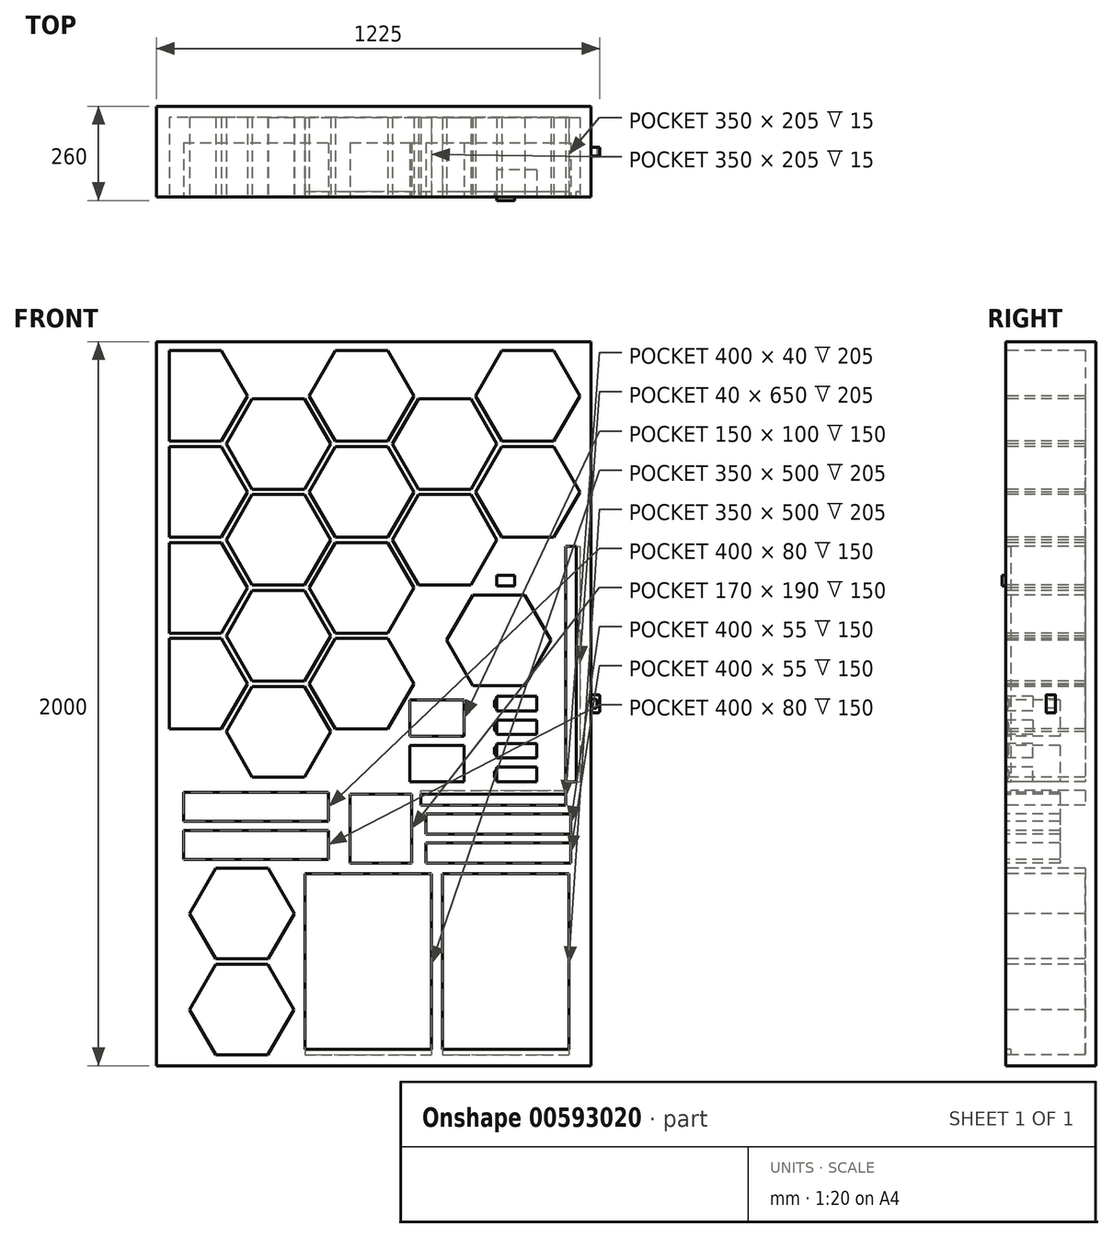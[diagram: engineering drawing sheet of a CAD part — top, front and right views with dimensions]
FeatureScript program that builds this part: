
annotation { "Feature Type Name" : "Feature", "Feature Type Description" : "" }
export const myFeature = defineFeature(function(context is Context, id is Id, definition is map)
    precondition{}
    {
        {
            var Q0;
            Q0=qCreatedBy(makeId("Top.planeOp"),FACE);
            var sketch = newSketch(context, id + "F0", { "sketchPlane" : qUnion([Q0])});
            skLineSegment(sketch, "E0.bottom", {"start": v(-593.08, -131.45) * mm, "end": v(606.92, -131.45) * mm});
            skLineSegment(sketch, "E0.top", {"start": v(-593.08, 118.55) * mm, "end": v(606.92, 118.55) * mm});
            skLineSegment(sketch, "E0.left", {"start": v(-593.08, -131.45) * mm, "end": v(-593.08, 118.55) * mm});
            skLineSegment(sketch, "E0.right", {"start": v(606.92, -131.45) * mm, "end": v(606.92, 118.55) * mm});
            skSolve(sketch);
        }
        {
            var Q0;
            Q0 = qSketchRegion(id + "F0", true);
            extrude(context, id + "F1", {"entities" : qUnion([Q0]), "depth" : 2000 * mm, "offsetDistance" : 25 * mm});
        }
        {
            var Q0;
            Q0=makeQuery(id+"F1.opExtrude","SWEPT_FACE",FACE,{"disambiguationData":[OSD([sQuery(id+"F0.wireOp",EDGE,"E0.bottom")])]});
            var sketch = newSketch(context, id + "F2", { "sketchPlane" : qUnion([Q0])});
            skLineSegment(sketch, "E1.right", {"start": v(576.92, 1435) * mm, "end": v(576.92, 785) * mm});
            skLineSegment(sketch, "E2", {"start": v(536.92, 1435) * mm, "end": v(576.92, 1435) * mm});
            skLineSegment(sketch, "E3", {"start": v(536.92, 1435) * mm, "end": v(536.92, 785) * mm});
            skLineSegment(sketch, "E4", {"start": v(536.92, 785) * mm, "end": v(576.92, 785) * mm});
            skLineSegment(sketch, "E5.bottom", {"start": v(136.92, 760) * mm, "end": v(536.92, 760) * mm});
            skLineSegment(sketch, "E5.top", {"start": v(136.92, 720) * mm, "end": v(536.92, 720) * mm});
            skLineSegment(sketch, "E5.left", {"start": v(136.92, 760) * mm, "end": v(136.92, 720) * mm});
            skLineSegment(sketch, "E5.right", {"start": v(536.92, 760) * mm, "end": v(536.92, 720) * mm});
            skSolve(sketch);
        }
        {
            var Q0;
            Q0 = qSketchRegion(id + "F2", true);
            extrude(context, id + "F3", {"entities" : qUnion([Q0]), "operationType" : NewBodyOperationType.REMOVE, "oppositeDirection" : true, "depth" : 220 * mm, "offsetDistance" : 25 * mm});
        }
        {
            var Q0;
            Q0=makeQuery(id+"F1.opExtrude","SWEPT_FACE",FACE,{"disambiguationData":[OSD([sQuery(id+"F0.wireOp",EDGE,"E0.right")])]});
            cPlane(context, id + "F4", {"entities" : qUnion([Q0]), "cplaneType" : CPlaneType.OFFSET, "offset" : 30 * mm, "oppositeDirection" : true, "width" : 150 * mm, "height" : 150 * mm});
        }
        {
            var Q0;
            Q0=qCreatedBy(id+"F4.planeOp",FACE);
            var sketch = newSketch(context, id + "F5", { "sketchPlane" : qUnion([Q0])});
            skLineSegment(sketch, "E6.bottom", {"start": v(-131.45, 1435) * mm, "end": v(-116.45, 1435) * mm});
            skLineSegment(sketch, "E6.top", {"start": v(-131.45, 785) * mm, "end": v(-116.45, 785) * mm});
            skLineSegment(sketch, "E6.left", {"start": v(-131.45, 1435) * mm, "end": v(-131.45, 785) * mm});
            skLineSegment(sketch, "E6.right", {"start": v(-116.45, 1435) * mm, "end": v(-116.45, 785) * mm});
            skSolve(sketch);
        }
        {
            var Q0;
            Q0 = qSketchRegion(id + "F5", true);
            extrude(context, id + "F6", {"entities" : qUnion([Q0]), "operationType" : NewBodyOperationType.ADD, "oppositeDirection" : true, "depth" : 10 * mm, "offsetDistance" : 25 * mm});
        }
        {
            var Q0;
            Q0=makeQuery(id+"F0.imprint","IMPRINT",FACE,{"disambiguationData":[TD([[makeQuery(id+"F0.imprint","IMPRINT",EDGE,{"derivedFrom":sQuery(id+"F0.wireOp",EDGE,"E0.bottom")}),1.0]])]});
            cPlane(context, id + "F7", {"entities" : qUnion([Q0]), "cplaneType" : CPlaneType.OFFSET, "offset" : 760 * mm, "width" : 150 * mm, "height" : 150 * mm});
        }
        {
            var Q0;
            Q0=qCreatedBy(id+"F7.planeOp",FACE);
            var sketch = newSketch(context, id + "F8", { "sketchPlane" : qUnion([Q0])});
            skLineSegment(sketch, "E7.bottom", {"start": v(136.92, -131.45) * mm, "end": v(536.92, -131.45) * mm});
            skLineSegment(sketch, "E7.top", {"start": v(136.92, -116.45) * mm, "end": v(536.92, -116.45) * mm});
            skLineSegment(sketch, "E7.left", {"start": v(136.92, -131.45) * mm, "end": v(136.92, -116.45) * mm});
            skLineSegment(sketch, "E7.right", {"start": v(536.92, -131.45) * mm, "end": v(536.92, -116.45) * mm});
            skSolve(sketch);
        }
        {
            var Q0;
            Q0 = qSketchRegion(id + "F8", true);
            extrude(context, id + "F9", {"entities" : qUnion([Q0]), "operationType" : NewBodyOperationType.ADD, "oppositeDirection" : true, "depth" : 10 * mm, "offsetDistance" : 25 * mm});
        }
        {
            var Q0;
            Q0=makeQuery(id+"F2.imprint","IMPRINT",FACE,{"disambiguationData":[TD([[makeQuery(id+"F2.imprint","IMPRINT",EDGE,{"derivedFrom":sQuery(id+"F2.wireOp",EDGE,"E1.right")}),1.0]])]});
            var sketch = newSketch(context, id + "F10", { "sketchPlane" : qUnion([Q0])});
            skLineSegment(sketch, "E8.bottom", {"start": v(456.92, 785) * mm, "end": v(346.92, 785) * mm});
            skLineSegment(sketch, "E8.top", {"start": v(456.92, 825) * mm, "end": v(346.92, 825) * mm});
            skLineSegment(sketch, "E8.left", {"start": v(456.92, 785) * mm, "end": v(456.92, 825) * mm});
            skLineSegment(sketch, "E8.right", {"start": v(346.92, 785) * mm, "end": v(346.92, 825) * mm});
            skSolve(sketch);
        }
        {
            var Q0;
            Q0=makeQuery(id+"F10.imprint","IMPRINT",FACE,{"disambiguationData":[TD([[makeQuery(id+"F10.imprint","IMPRINT",EDGE,{"derivedFrom":sQuery(id+"F10.wireOp",EDGE,"E8.bottom")}),-1.0]])]});
            extrude(context, id + "F11", {"entities" : qUnion([Q0]), "operationType" : NewBodyOperationType.REMOVE, "oppositeDirection" : true, "depth" : 75 * mm, "offsetDistance" : 25 * mm});
        }
        {
            var Q0;
            Q0=makeQuery(id+"F0.imprint","IMPRINT",FACE,{"disambiguationData":[TD([[makeQuery(id+"F0.imprint","IMPRINT",EDGE,{"derivedFrom":sQuery(id+"F0.wireOp",EDGE,"E0.bottom")}),1.0]])]});
            cPlane(context, id + "F12", {"entities" : qUnion([Q0]), "cplaneType" : CPlaneType.OFFSET, "offset" : 805 * mm, "width" : 150 * mm, "height" : 150 * mm});
        }
        {
            var Q0;
            Q0=qCreatedBy(id+"F12.planeOp",FACE);
            var sketch = newSketch(context, id + "F13", { "sketchPlane" : qUnion([Q0])});
            skArc(sketch, "E9", {"start": v(346.92, -123.45) * mm, "mid": v(338.92, -127.45) * mm, "end": v(346.92, -131.45) * mm});
            skLineSegment(sketch, "E10.bottom", {"start": v(346.92, -123.45) * mm, "end": v(351.44, -123.45) * mm});
            skLineSegment(sketch, "E10.top", {"start": v(346.92, -131.45) * mm, "end": v(351.44, -131.45) * mm});
            skLineSegment(sketch, "E10.right", {"start": v(351.44, -123.45) * mm, "end": v(351.44, -131.45) * mm});
            skSolve(sketch);
        }
        {
            var Q0;
            Q0 = qSketchRegion(id + "F13", true);
            var Q1;
            Q1=sQuery(id+"F13.wireOp",EDGE,"E9");
            var Q2;
            Q2=sQuery(id+"F13.wireOp",EDGE,"wPp1E5a5-Cfel-xhtf-EEdg-7zQgNDPYHGg3");
            extrude(context, id + "F14", {"entities" : qUnion([Q0]), "operationType" : NewBodyOperationType.REMOVE, "surfaceEntities" : qUnion([Q1, Q2]), "endBound" : BoundingType.SYMMETRIC, "oppositeDirection" : true, "depth" : 18 * mm, "offsetDistance" : 25 * mm, "hasDraft" : true, "draftAngle" : 0 * degree});
        }
        {
            var Q0;
            Q0=makeQuery(id+"F0.imprint","IMPRINT",FACE,{"disambiguationData":[TD([[makeQuery(id+"F0.imprint","IMPRINT",EDGE,{"derivedFrom":sQuery(id+"F0.wireOp",EDGE,"E0.bottom")}),1.0]])]});
            cPlane(context, id + "F15", {"entities" : qUnion([Q0]), "cplaneType" : CPlaneType.OFFSET, "offset" : 814 * mm, "width" : 150 * mm, "height" : 150 * mm});
        }
        {
            var Q0;
            Q0=makeQuery(id+"F0.imprint","IMPRINT",FACE,{"disambiguationData":[TD([[makeQuery(id+"F0.imprint","IMPRINT",EDGE,{"derivedFrom":sQuery(id+"F0.wireOp",EDGE,"E0.bottom")}),1.0]])]});
            cPlane(context, id + "F16", {"entities" : qUnion([Q0]), "cplaneType" : CPlaneType.OFFSET, "offset" : 796 * mm, "width" : 150 * mm, "height" : 150 * mm});
        }
        {
            var Q0;
            Q0=qCreatedBy(id+"F15.planeOp",FACE);
            var sketch = newSketch(context, id + "F17", { "sketchPlane" : qUnion([Q0])});
            skCircle(sketch, "E11", {"center": v(343.92, -127.45) * mm, "radius": 2.25 * mm});
            skSolve(sketch);
        }
        {
            var Q0;
            Q0 = qSketchRegion(id + "F17", true);
            extrude(context, id + "F18", {"entities" : qUnion([Q0]), "operationType" : NewBodyOperationType.REMOVE, "depth" : 5 * mm, "offsetDistance" : 25 * mm});
        }
        {
            var Q0;
            Q0=qCreatedBy(id+"F16.planeOp",FACE);
            var sketch = newSketch(context, id + "F19", { "sketchPlane" : qUnion([Q0])});
            skCircle(sketch, "E12", {"center": v(343.92, -127.45) * mm, "radius": 2.25 * mm});
            skSolve(sketch);
        }
        {
            var Q0;
            Q0 = qSketchRegion(id + "F19", true);
            extrude(context, id + "F20", {"entities" : qUnion([Q0]), "operationType" : NewBodyOperationType.REMOVE, "oppositeDirection" : true, "depth" : 5 * mm, "offsetDistance" : 25 * mm});
        }
        {
            var Q0;
            Q0=makeQuery(id+"F2.imprint","IMPRINT",FACE,{"disambiguationData":[TD([[makeQuery(id+"F2.imprint","IMPRINT",EDGE,{"derivedFrom":sQuery(id+"F2.wireOp",EDGE,"E1.right")}),1.0]])]});
            var sketch = newSketch(context, id + "F21", { "sketchPlane" : qUnion([Q0])});
            skLineSegment(sketch, "E13.bottom", {"start": v(456.92, 850) * mm, "end": v(346.92, 850) * mm});
            skLineSegment(sketch, "E13.top", {"start": v(456.92, 890) * mm, "end": v(346.92, 890) * mm});
            skLineSegment(sketch, "E13.left", {"start": v(456.92, 850) * mm, "end": v(456.92, 890) * mm});
            skLineSegment(sketch, "E13.right", {"start": v(346.92, 850) * mm, "end": v(346.92, 890) * mm});
            skSolve(sketch);
        }
        {
            var Q0;
            Q0 = qSketchRegion(id + "F21", true);
            var Q1;
            Q1=sQuery(id+"F21.wireOp",EDGE,"E13.top");
            extrude(context, id + "F22", {"entities" : qUnion([Q0]), "operationType" : NewBodyOperationType.REMOVE, "surfaceEntities" : qUnion([Q1]), "oppositeDirection" : true, "depth" : 75 * mm, "offsetDistance" : 25 * mm});
        }
        {
            var Q0;
            Q0=makeQuery(id+"F0.imprint","IMPRINT",FACE,{"disambiguationData":[TD([[makeQuery(id+"F0.imprint","IMPRINT",EDGE,{"derivedFrom":sQuery(id+"F0.wireOp",EDGE,"E0.bottom")}),1.0]])]});
            cPlane(context, id + "F23", {"entities" : qUnion([Q0]), "cplaneType" : CPlaneType.OFFSET, "offset" : 870 * mm, "width" : 150 * mm, "height" : 150 * mm});
        }
        {
            var Q0;
            Q0=qCreatedBy(id+"F23.planeOp",FACE);
            var sketch = newSketch(context, id + "F24", { "sketchPlane" : qUnion([Q0])});
            skArc(sketch, "E14", {"start": v(346.92, -123.45) * mm, "mid": v(338.92, -127.45) * mm, "end": v(346.92, -131.45) * mm});
            skLineSegment(sketch, "E15.bottom", {"start": v(346.92, -123.45) * mm, "end": v(351.44, -123.45) * mm});
            skLineSegment(sketch, "E15.top", {"start": v(346.92, -131.45) * mm, "end": v(351.44, -131.45) * mm});
            skLineSegment(sketch, "E15.right", {"start": v(351.44, -123.45) * mm, "end": v(351.44, -131.45) * mm});
            skSolve(sketch);
        }
        {
            var Q0;
            Q0 = qSketchRegion(id + "F24", true);
            extrude(context, id + "F25", {"entities" : qUnion([Q0]), "operationType" : NewBodyOperationType.REMOVE, "endBound" : BoundingType.SYMMETRIC, "oppositeDirection" : true, "depth" : 18 * mm, "offsetDistance" : 25 * mm});
        }
        {
            var Q0;
            Q0=makeQuery(id+"F0.imprint","IMPRINT",FACE,{"disambiguationData":[TD([[makeQuery(id+"F0.imprint","IMPRINT",EDGE,{"derivedFrom":sQuery(id+"F0.wireOp",EDGE,"E0.bottom")}),1.0]])]});
            cPlane(context, id + "F26", {"entities" : qUnion([Q0]), "cplaneType" : CPlaneType.OFFSET, "offset" : 879 * mm, "width" : 150 * mm, "height" : 150 * mm});
        }
        {
            var Q0;
            Q0=makeQuery(id+"F0.imprint","IMPRINT",FACE,{"disambiguationData":[TD([[makeQuery(id+"F0.imprint","IMPRINT",EDGE,{"derivedFrom":sQuery(id+"F0.wireOp",EDGE,"E0.bottom")}),1.0]])]});
            cPlane(context, id + "F27", {"entities" : qUnion([Q0]), "cplaneType" : CPlaneType.OFFSET, "offset" : 861 * mm, "width" : 150 * mm, "height" : 150 * mm});
        }
        {
            var Q0;
            Q0=qCreatedBy(id+"F26.planeOp",FACE);
            var sketch = newSketch(context, id + "F28", { "sketchPlane" : qUnion([Q0])});
            skCircle(sketch, "E16", {"center": v(343.92, -127.45) * mm, "radius": 2.25 * mm});
            skSolve(sketch);
        }
        {
            var Q0;
            Q0 = qSketchRegion(id + "F28", true);
            extrude(context, id + "F29", {"entities" : qUnion([Q0]), "operationType" : NewBodyOperationType.REMOVE, "depth" : 5 * mm, "offsetDistance" : 25 * mm});
        }
        {
            var Q0;
            Q0=qCreatedBy(id+"F27.planeOp",FACE);
            var sketch = newSketch(context, id + "F30", { "sketchPlane" : qUnion([Q0])});
            skCircle(sketch, "E17", {"center": v(343.92, -127.45) * mm, "radius": 2.25 * mm});
            skSolve(sketch);
        }
        {
            var Q0;
            Q0 = qSketchRegion(id + "F30", true);
            extrude(context, id + "F31", {"entities" : qUnion([Q0]), "operationType" : NewBodyOperationType.REMOVE, "oppositeDirection" : true, "depth" : 5 * mm, "offsetDistance" : 25 * mm});
        }
        {
            var Q0;
            Q0=makeQuery(id+"F2.imprint","IMPRINT",FACE,{"disambiguationData":[TD([[makeQuery(id+"F2.imprint","IMPRINT",EDGE,{"derivedFrom":sQuery(id+"F2.wireOp",EDGE,"E1.right")}),1.0]])]});
            var sketch = newSketch(context, id + "F32", { "sketchPlane" : qUnion([Q0])});
            skLineSegment(sketch, "E18.bottom", {"start": v(346.92, 955) * mm, "end": v(456.92, 955) * mm});
            skLineSegment(sketch, "E18.top", {"start": v(346.92, 915) * mm, "end": v(456.92, 915) * mm});
            skLineSegment(sketch, "E18.left", {"start": v(346.92, 955) * mm, "end": v(346.92, 915) * mm});
            skLineSegment(sketch, "E18.right", {"start": v(456.92, 955) * mm, "end": v(456.92, 915) * mm});
            skSolve(sketch);
        }
        {
            var Q0;
            Q0 = qSketchRegion(id + "F32", true);
            extrude(context, id + "F33", {"entities" : qUnion([Q0]), "operationType" : NewBodyOperationType.REMOVE, "oppositeDirection" : true, "depth" : 75 * mm, "offsetDistance" : 25 * mm});
        }
        {
            var Q0;
            Q0=makeQuery(id+"F0.imprint","IMPRINT",FACE,{"disambiguationData":[TD([[makeQuery(id+"F0.imprint","IMPRINT",EDGE,{"derivedFrom":sQuery(id+"F0.wireOp",EDGE,"E0.bottom")}),1.0]])]});
            cPlane(context, id + "F34", {"entities" : qUnion([Q0]), "cplaneType" : CPlaneType.OFFSET, "offset" : 935 * mm, "width" : 150 * mm, "height" : 150 * mm});
        }
        {
            var Q0;
            Q0=qCreatedBy(id+"F34.planeOp",FACE);
            var sketch = newSketch(context, id + "F35", { "sketchPlane" : qUnion([Q0])});
            skArc(sketch, "E19", {"start": v(346.92, -123.45) * mm, "mid": v(338.92, -127.45) * mm, "end": v(346.92, -131.45) * mm});
            skLineSegment(sketch, "E20", {"start": v(346.92, -123.45) * mm, "end": v(346.92, -131.45) * mm});
            skSolve(sketch);
        }
        {
            var Q0;
            Q0 = qSketchRegion(id + "F35", true);
            extrude(context, id + "F36", {"entities" : qUnion([Q0]), "operationType" : NewBodyOperationType.REMOVE, "endBound" : BoundingType.SYMMETRIC, "oppositeDirection" : true, "depth" : 18 * mm, "offsetDistance" : 25 * mm});
        }
        {
            var Q0;
            Q0=makeQuery(id+"F0.imprint","IMPRINT",FACE,{"disambiguationData":[TD([[makeQuery(id+"F0.imprint","IMPRINT",EDGE,{"derivedFrom":sQuery(id+"F0.wireOp",EDGE,"E0.bottom")}),1.0]])]});
            cPlane(context, id + "F37", {"entities" : qUnion([Q0]), "cplaneType" : CPlaneType.OFFSET, "offset" : 944 * mm, "width" : 150 * mm, "height" : 150 * mm});
        }
        {
            var Q0;
            Q0=makeQuery(id+"F0.imprint","IMPRINT",FACE,{"disambiguationData":[TD([[makeQuery(id+"F0.imprint","IMPRINT",EDGE,{"derivedFrom":sQuery(id+"F0.wireOp",EDGE,"E0.bottom")}),1.0]])]});
            cPlane(context, id + "F38", {"entities" : qUnion([Q0]), "cplaneType" : CPlaneType.OFFSET, "offset" : 926 * mm, "width" : 150 * mm, "height" : 150 * mm});
        }
        {
            var Q0;
            Q0=qCreatedBy(id+"F37.planeOp",FACE);
            var sketch = newSketch(context, id + "F39", { "sketchPlane" : qUnion([Q0])});
            skCircle(sketch, "E21", {"center": v(343.92, -127.45) * mm, "radius": 2.25 * mm});
            skSolve(sketch);
        }
        {
            var Q0;
            Q0 = qSketchRegion(id + "F39", true);
            extrude(context, id + "F40", {"entities" : qUnion([Q0]), "operationType" : NewBodyOperationType.REMOVE, "depth" : 5 * mm, "offsetDistance" : 25 * mm});
        }
        {
            var Q0;
            Q0=qCreatedBy(id+"F38.planeOp",FACE);
            var sketch = newSketch(context, id + "F41", { "sketchPlane" : qUnion([Q0])});
            skCircle(sketch, "E22", {"center": v(343.92, -127.45) * mm, "radius": 2.25 * mm});
            skSolve(sketch);
        }
        {
            var Q0;
            Q0 = qSketchRegion(id + "F41", true);
            extrude(context, id + "F42", {"entities" : qUnion([Q0]), "operationType" : NewBodyOperationType.REMOVE, "oppositeDirection" : true, "depth" : 5 * mm, "offsetDistance" : 25 * mm});
        }
        {
            var Q0;
            Q0=makeQuery(id+"F2.imprint","IMPRINT",FACE,{"disambiguationData":[TD([[makeQuery(id+"F2.imprint","IMPRINT",EDGE,{"derivedFrom":sQuery(id+"F2.wireOp",EDGE,"E1.right")}),1.0]])]});
            var sketch = newSketch(context, id + "F43", { "sketchPlane" : qUnion([Q0])});
            skLineSegment(sketch, "E23.bottom", {"start": v(546.92, 30) * mm, "end": v(196.92, 30) * mm});
            skLineSegment(sketch, "E23.top", {"start": v(546.92, 530) * mm, "end": v(196.92, 530) * mm});
            skLineSegment(sketch, "E23.left", {"start": v(546.92, 30) * mm, "end": v(546.92, 530) * mm});
            skLineSegment(sketch, "E23.right", {"start": v(196.92, 30) * mm, "end": v(196.92, 530) * mm});
            skLineSegment(sketch, "E24.bottom", {"start": v(-183.08, 530) * mm, "end": v(166.92, 530) * mm});
            skLineSegment(sketch, "E24.top", {"start": v(-183.08, 30) * mm, "end": v(166.92, 30) * mm});
            skLineSegment(sketch, "E24.left", {"start": v(-183.08, 530) * mm, "end": v(-183.08, 30) * mm});
            skLineSegment(sketch, "E24.right", {"start": v(166.92, 530) * mm, "end": v(166.92, 30) * mm});
            skSolve(sketch);
        }
        {
            var Q0;
            Q0=makeQuery(id+"F43.imprint","IMPRINT",FACE,{"disambiguationData":[TD([[makeQuery(id+"F43.imprint","IMPRINT",EDGE,{"derivedFrom":sQuery(id+"F43.wireOp",EDGE,"E23.bottom")}),1.0]])]});
            var sketch = newSketch(context, id + "F44", { "sketchPlane" : qUnion([Q0])});
            skLineSegment(sketch, "E25.bottom", {"start": v(106.92, 1010) * mm, "end": v(256.92, 1010) * mm});
            skLineSegment(sketch, "E25.top", {"start": v(106.92, 785) * mm, "end": v(256.92, 785) * mm});
            skLineSegment(sketch, "E25.left", {"start": v(106.92, 1010) * mm, "end": v(106.92, 910) * mm});
            skLineSegment(sketch, "E25.right", {"start": v(256.92, 1010) * mm, "end": v(256.92, 910) * mm});
            skLineSegment(sketch, "E26", {"start": v(256.92, 910) * mm, "end": v(106.92, 910) * mm});
            skLineSegment(sketch, "E27", {"start": v(106.92, 885) * mm, "end": v(256.92, 885) * mm});
            skLineSegment(sketch, "E28.trimOffspring", {"start": v(106.92, 885) * mm, "end": v(106.92, 785) * mm});
            skLineSegment(sketch, "E29.trimOffspring", {"start": v(256.92, 885) * mm, "end": v(256.92, 785) * mm});
            skSolve(sketch);
        }
        {
            var Q0;
            Q0=makeQuery(id+"F44.imprint","IMPRINT",FACE,{"disambiguationData":[TD([[makeQuery(id+"F44.imprint","IMPRINT",EDGE,{"derivedFrom":sQuery(id+"F44.wireOp",EDGE,"E25.bottom")}),-1.0]])]});
            var Q1;
            Q1=makeQuery(id+"F44.imprint","IMPRINT",FACE,{"disambiguationData":[TD([[makeQuery(id+"F44.imprint","IMPRINT",EDGE,{"derivedFrom":sQuery(id+"F44.wireOp",EDGE,"E25.top")}),1.0]])]});
            extrude(context, id + "F45", {"entities" : qUnion([Q0, Q1]), "operationType" : NewBodyOperationType.REMOVE, "oppositeDirection" : true, "depth" : 150 * mm, "offsetDistance" : 25 * mm});
        }
        {
            var Q0;
            Q0=makeQuery(id+"F2.imprint","IMPRINT",FACE,{"disambiguationData":[TD([[makeQuery(id+"F2.imprint","IMPRINT",EDGE,{"derivedFrom":sQuery(id+"F2.wireOp",EDGE,"E1.right")}),1.0]])]});
            var sketch = newSketch(context, id + "F46", { "sketchPlane" : qUnion([Q0])});
            skCircle(sketch, "E30.cCircle", {"center": v(352.58, 1175) * mm, "radius": 125 * mm, "construction": true});
            skLineSegment(sketch, "E30.0", {"start": v(496.92, 1175) * mm, "end": v(424.75, 1050) * mm});
            skLineSegment(sketch, "E30.1", {"start": v(424.75, 1050) * mm, "end": v(280.4, 1050) * mm});
            skLineSegment(sketch, "E30.2", {"start": v(280.4, 1050) * mm, "end": v(208.24, 1175) * mm});
            skLineSegment(sketch, "E30.3", {"start": v(208.24, 1175) * mm, "end": v(280.4, 1300) * mm});
            skLineSegment(sketch, "E30.4", {"start": v(280.4, 1300) * mm, "end": v(424.75, 1300) * mm});
            skLineSegment(sketch, "E30.5", {"start": v(424.75, 1300) * mm, "end": v(496.92, 1175) * mm});
            skPoint(sketch, "E30.0.midPoint", {"position": v(460.83, 1112.5) * mm});
            skSolve(sketch);
        }
        {
            var Q0;
            Q0=makeQuery(id+"F46.imprint","IMPRINT",FACE,{"disambiguationData":[TD([[makeQuery(id+"F46.imprint","IMPRINT",EDGE,{"derivedFrom":sQuery(id+"F46.wireOp",EDGE,"E30.0")}),-1.0]])]});
            extrude(context, id + "F47", {"entities" : qUnion([Q0]), "operationType" : NewBodyOperationType.REMOVE, "oppositeDirection" : true, "depth" : 220 * mm, "offsetDistance" : 25 * mm});
        }
        {
            var Q0;
            Q0=makeQuery(id+"F0.imprint","IMPRINT",FACE,{"disambiguationData":[TD([[makeQuery(id+"F0.imprint","IMPRINT",EDGE,{"derivedFrom":sQuery(id+"F0.wireOp",EDGE,"E0.bottom")}),1.0]])]});
            cPlane(context, id + "F48", {"entities" : qUnion([Q0]), "cplaneType" : CPlaneType.OFFSET, "offset" : 1000 * mm, "width" : 150 * mm, "height" : 150 * mm});
        }
        {
            var Q0;
            Q0=makeQuery(id+"F2.imprint","IMPRINT",FACE,{"disambiguationData":[TD([[makeQuery(id+"F2.imprint","IMPRINT",EDGE,{"derivedFrom":sQuery(id+"F2.wireOp",EDGE,"E1.right")}),1.0]])]});
            var sketch = newSketch(context, id + "F49", { "sketchPlane" : qUnion([Q0])});
            skLineSegment(sketch, "E31.bottom", {"start": v(346.92, 1020) * mm, "end": v(456.92, 1020) * mm});
            skLineSegment(sketch, "E31.top", {"start": v(346.92, 980) * mm, "end": v(456.92, 980) * mm});
            skLineSegment(sketch, "E31.left", {"start": v(346.92, 1020) * mm, "end": v(346.92, 980) * mm});
            skLineSegment(sketch, "E31.right", {"start": v(456.92, 1020) * mm, "end": v(456.92, 980) * mm});
            skSolve(sketch);
        }
        {
            var Q0;
            Q0 = qSketchRegion(id + "F49", true);
            extrude(context, id + "F50", {"entities" : qUnion([Q0]), "operationType" : NewBodyOperationType.REMOVE, "oppositeDirection" : true, "depth" : 75 * mm, "offsetDistance" : 25 * mm});
        }
        {
            var Q0;
            Q0=qCreatedBy(id+"F48.planeOp",FACE);
            var sketch = newSketch(context, id + "F51", { "sketchPlane" : qUnion([Q0])});
            skArc(sketch, "E32", {"start": v(346.92, -123.45) * mm, "mid": v(338.92, -127.45) * mm, "end": v(346.92, -131.45) * mm});
            skLineSegment(sketch, "E33", {"start": v(346.92, -123.45) * mm, "end": v(346.92, -131.45) * mm});
            skSolve(sketch);
        }
        {
            var Q0;
            Q0 = qSketchRegion(id + "F51", true);
            extrude(context, id + "F52", {"entities" : qUnion([Q0]), "operationType" : NewBodyOperationType.REMOVE, "endBound" : BoundingType.SYMMETRIC, "depth" : 18 * mm, "offsetDistance" : 25 * mm});
        }
        {
            var Q0;
            Q0=makeQuery(id+"F0.imprint","IMPRINT",FACE,{"disambiguationData":[TD([[makeQuery(id+"F0.imprint","IMPRINT",EDGE,{"derivedFrom":sQuery(id+"F0.wireOp",EDGE,"E0.bottom")}),1.0]])]});
            cPlane(context, id + "F53", {"entities" : qUnion([Q0]), "cplaneType" : CPlaneType.OFFSET, "offset" : 1009 * mm, "width" : 150 * mm, "height" : 150 * mm});
        }
        {
            var Q0;
            Q0=makeQuery(id+"F0.imprint","IMPRINT",FACE,{"disambiguationData":[TD([[makeQuery(id+"F0.imprint","IMPRINT",EDGE,{"derivedFrom":sQuery(id+"F0.wireOp",EDGE,"E0.bottom")}),1.0]])]});
            cPlane(context, id + "F54", {"entities" : qUnion([Q0]), "cplaneType" : CPlaneType.OFFSET, "offset" : 991 * mm, "width" : 150 * mm, "height" : 150 * mm});
        }
        {
            var Q0;
            Q0=qCreatedBy(id+"F53.planeOp",FACE);
            var sketch = newSketch(context, id + "F55", { "sketchPlane" : qUnion([Q0])});
            skCircle(sketch, "E34", {"center": v(343.92, -127.45) * mm, "radius": 2.25 * mm});
            skSolve(sketch);
        }
        {
            var Q0;
            Q0 = qSketchRegion(id + "F55", true);
            extrude(context, id + "F56", {"entities" : qUnion([Q0]), "operationType" : NewBodyOperationType.REMOVE, "depth" : 5 * mm, "offsetDistance" : 25 * mm});
        }
        {
            var Q0;
            Q0=qCreatedBy(id+"F54.planeOp",FACE);
            var sketch = newSketch(context, id + "F57", { "sketchPlane" : qUnion([Q0])});
            skCircle(sketch, "E35", {"center": v(343.92, -127.45) * mm, "radius": 2.25 * mm});
            skSolve(sketch);
        }
        {
            var Q0;
            Q0 = qSketchRegion(id + "F57", true);
            extrude(context, id + "F58", {"entities" : qUnion([Q0]), "operationType" : NewBodyOperationType.REMOVE, "oppositeDirection" : true, "depth" : 5 * mm, "offsetDistance" : 25 * mm});
        }
        {
            var Q0;
            Q0=makeQuery(id+"F10.imprint","IMPRINT",FACE,{"disambiguationData":[TD([[makeQuery(id+"F10.imprint","IMPRINT",EDGE,{"derivedFrom":sQuery(id+"F10.wireOp",EDGE,"E8.bottom")}),1.0]])]});
            var sketch = newSketch(context, id + "F59", { "sketchPlane" : qUnion([Q0])});
            skLineSegment(sketch, "E36.bottom", {"start": v(346.92, 1355) * mm, "end": v(396.92, 1355) * mm});
            skLineSegment(sketch, "E36.top", {"start": v(346.92, 1325) * mm, "end": v(396.92, 1325) * mm});
            skLineSegment(sketch, "E36.left", {"start": v(346.92, 1355) * mm, "end": v(346.92, 1325) * mm});
            skLineSegment(sketch, "E36.right", {"start": v(396.92, 1355) * mm, "end": v(396.92, 1325) * mm});
            skSolve(sketch);
        }
        {
            var Q0;
            Q0 = qSketchRegion(id + "F59", true);
            extrude(context, id + "F60", {"entities" : qUnion([Q0]), "operationType" : NewBodyOperationType.ADD, "depth" : 10 * mm, "offsetDistance" : 25 * mm});
        }
        {
            var Q0;
            Q0 = qSketchRegion(id + "F43", true);
            extrude(context, id + "F61", {"entities" : qUnion([Q0]), "operationType" : NewBodyOperationType.REMOVE, "oppositeDirection" : true, "depth" : 220 * mm, "offsetDistance" : 25 * mm});
        }
        {
            var Q0;
            Q0=makeQuery(id+"F0.imprint","IMPRINT",FACE,{"disambiguationData":[TD([[makeQuery(id+"F0.imprint","IMPRINT",EDGE,{"derivedFrom":sQuery(id+"F0.wireOp",EDGE,"E0.bottom")}),1.0]])]});
            cPlane(context, id + "F62", {"entities" : qUnion([Q0]), "cplaneType" : CPlaneType.OFFSET, "offset" : 30 * mm, "width" : 150 * mm, "height" : 150 * mm});
        }
        {
            var Q0;
            Q0=qCreatedBy(id+"F62.planeOp",FACE);
            var sketch = newSketch(context, id + "F63", { "sketchPlane" : qUnion([Q0])});
            skLineSegment(sketch, "E37.bottom", {"start": v(-183.08, -116.45) * mm, "end": v(166.92, -116.45) * mm});
            skLineSegment(sketch, "E37.top", {"start": v(-183.08, -131.45) * mm, "end": v(166.92, -131.45) * mm});
            skLineSegment(sketch, "E37.left", {"start": v(-183.08, -116.45) * mm, "end": v(-183.08, -131.45) * mm});
            skLineSegment(sketch, "E37.right", {"start": v(166.92, -116.45) * mm, "end": v(166.92, -131.45) * mm});
            skLineSegment(sketch, "E38.bottom", {"start": v(196.92, -116.45) * mm, "end": v(546.92, -116.45) * mm});
            skLineSegment(sketch, "E38.top", {"start": v(196.92, -131.45) * mm, "end": v(546.92, -131.45) * mm});
            skLineSegment(sketch, "E38.left", {"start": v(196.92, -116.45) * mm, "end": v(196.92, -131.45) * mm});
            skLineSegment(sketch, "E38.right", {"start": v(546.92, -116.45) * mm, "end": v(546.92, -131.45) * mm});
            skSolve(sketch);
        }
        {
            var Q0;
            Q0 = qSketchRegion(id + "F63", true);
            extrude(context, id + "F64", {"entities" : qUnion([Q0]), "operationType" : NewBodyOperationType.ADD, "depth" : 15 * mm, "offsetDistance" : 25 * mm});
        }
        {
            var Q0;
            Q0=makeQuery(id+"F2.imprint","IMPRINT",FACE,{"disambiguationData":[TD([[makeQuery(id+"F2.imprint","IMPRINT",EDGE,{"derivedFrom":sQuery(id+"F2.wireOp",EDGE,"E1.right")}),1.0]])]});
            var sketch = newSketch(context, id + "F65", { "sketchPlane" : qUnion([Q0])});
            skCircle(sketch, "E39.cCircle", {"center": v(432.58, 1850) * mm, "radius": 125 * mm, "construction": true});
            skLineSegment(sketch, "E39.0", {"start": v(360.4, 1975) * mm, "end": v(288.24, 1850) * mm});
            skLineSegment(sketch, "E39.1", {"start": v(504.75, 1975) * mm, "end": v(360.4, 1975) * mm});
            skLineSegment(sketch, "E39.2", {"start": v(576.92, 1850) * mm, "end": v(504.75, 1975) * mm});
            skLineSegment(sketch, "E39.3", {"start": v(504.75, 1725) * mm, "end": v(576.92, 1850) * mm});
            skLineSegment(sketch, "E39.4", {"start": v(360.4, 1725) * mm, "end": v(504.75, 1725) * mm});
            skLineSegment(sketch, "E39.5", {"start": v(288.24, 1850) * mm, "end": v(360.4, 1725) * mm});
            skPoint(sketch, "E39.0.midPoint", {"position": v(324.32, 1912.5) * mm});
            skCircle(sketch, "E40.cCircle", {"center": v(203.08, 1717.5) * mm, "radius": 125 * mm, "construction": true});
            skLineSegment(sketch, "E40.0", {"start": v(130.91, 1842.5) * mm, "end": v(58.74, 1717.5) * mm});
            skLineSegment(sketch, "E40.1", {"start": v(275.25, 1842.5) * mm, "end": v(130.91, 1842.5) * mm});
            skLineSegment(sketch, "E40.2", {"start": v(347.42, 1717.5) * mm, "end": v(275.25, 1842.5) * mm});
            skLineSegment(sketch, "E40.3", {"start": v(275.25, 1592.5) * mm, "end": v(347.42, 1717.5) * mm});
            skLineSegment(sketch, "E40.4", {"start": v(130.91, 1592.5) * mm, "end": v(275.25, 1592.5) * mm});
            skLineSegment(sketch, "E40.5", {"start": v(58.74, 1717.5) * mm, "end": v(130.91, 1592.5) * mm});
            skPoint(sketch, "E40.0.midPoint", {"position": v(94.83, 1780) * mm});
            skCircle(sketch, "E41.cCircle", {"center": v(432.58, 1585) * mm, "radius": 125 * mm, "construction": true});
            skLineSegment(sketch, "E41.0", {"start": v(360.4, 1710) * mm, "end": v(288.24, 1585) * mm});
            skLineSegment(sketch, "E41.1", {"start": v(504.75, 1710) * mm, "end": v(360.4, 1710) * mm});
            skLineSegment(sketch, "E41.2", {"start": v(576.92, 1585) * mm, "end": v(504.75, 1710) * mm});
            skLineSegment(sketch, "E41.3", {"start": v(504.75, 1460) * mm, "end": v(576.92, 1585) * mm});
            skLineSegment(sketch, "E41.4", {"start": v(360.4, 1460) * mm, "end": v(504.75, 1460) * mm});
            skLineSegment(sketch, "E41.5", {"start": v(288.24, 1585) * mm, "end": v(360.4, 1460) * mm});
            skPoint(sketch, "E41.0.midPoint", {"position": v(324.32, 1647.5) * mm});
            skCircle(sketch, "E42.cCircle", {"center": v(203.08, 1452.5) * mm, "radius": 125 * mm, "construction": true});
            skLineSegment(sketch, "E42.0", {"start": v(130.91, 1577.5) * mm, "end": v(58.74, 1452.5) * mm});
            skLineSegment(sketch, "E42.1", {"start": v(275.25, 1577.5) * mm, "end": v(130.91, 1577.5) * mm});
            skLineSegment(sketch, "E42.2", {"start": v(347.42, 1452.5) * mm, "end": v(275.25, 1577.5) * mm});
            skLineSegment(sketch, "E42.3", {"start": v(275.25, 1327.5) * mm, "end": v(347.42, 1452.5) * mm});
            skLineSegment(sketch, "E42.4", {"start": v(130.91, 1327.5) * mm, "end": v(275.25, 1327.5) * mm});
            skLineSegment(sketch, "E42.5", {"start": v(58.74, 1452.5) * mm, "end": v(130.91, 1327.5) * mm});
            skPoint(sketch, "E42.0.midPoint", {"position": v(94.83, 1515) * mm});
            skCircle(sketch, "E43.cCircle", {"center": v(-26.42, 1850) * mm, "radius": 125 * mm, "construction": true});
            skLineSegment(sketch, "E43.0", {"start": v(-98.58, 1975) * mm, "end": v(-170.75, 1850) * mm});
            skLineSegment(sketch, "E43.1", {"start": v(45.75, 1975) * mm, "end": v(-98.58, 1975) * mm});
            skLineSegment(sketch, "E43.2", {"start": v(117.92, 1850) * mm, "end": v(45.75, 1975) * mm});
            skLineSegment(sketch, "E43.3", {"start": v(45.75, 1725) * mm, "end": v(117.92, 1850) * mm});
            skLineSegment(sketch, "E43.4", {"start": v(-98.58, 1725) * mm, "end": v(45.75, 1725) * mm});
            skLineSegment(sketch, "E43.5", {"start": v(-170.75, 1850) * mm, "end": v(-98.58, 1725) * mm});
            skPoint(sketch, "E43.0.midPoint", {"position": v(-134.67, 1912.5) * mm});
            skCircle(sketch, "E44.cCircle", {"center": v(-26.42, 1585) * mm, "radius": 125 * mm, "construction": true});
            skLineSegment(sketch, "E44.0", {"start": v(-98.58, 1710) * mm, "end": v(-170.75, 1585) * mm});
            skLineSegment(sketch, "E44.1", {"start": v(45.75, 1710) * mm, "end": v(-98.58, 1710) * mm});
            skLineSegment(sketch, "E44.2", {"start": v(117.92, 1585) * mm, "end": v(45.75, 1710) * mm});
            skLineSegment(sketch, "E44.3", {"start": v(45.75, 1460) * mm, "end": v(117.92, 1585) * mm});
            skLineSegment(sketch, "E44.4", {"start": v(-98.58, 1460) * mm, "end": v(45.75, 1460) * mm});
            skLineSegment(sketch, "E44.5", {"start": v(-170.75, 1585) * mm, "end": v(-98.58, 1460) * mm});
            skPoint(sketch, "E44.0.midPoint", {"position": v(-134.67, 1647.5) * mm});
            skCircle(sketch, "E45.cCircle", {"center": v(-255.91, 1717.5) * mm, "radius": 125 * mm, "construction": true});
            skLineSegment(sketch, "E45.0", {"start": v(-328.08, 1842.5) * mm, "end": v(-400.25, 1717.5) * mm});
            skLineSegment(sketch, "E45.1", {"start": v(-183.74, 1842.5) * mm, "end": v(-328.08, 1842.5) * mm});
            skLineSegment(sketch, "E45.2", {"start": v(-111.58, 1717.5) * mm, "end": v(-183.74, 1842.5) * mm});
            skLineSegment(sketch, "E45.3", {"start": v(-183.74, 1592.5) * mm, "end": v(-111.58, 1717.5) * mm});
            skLineSegment(sketch, "E45.4", {"start": v(-328.08, 1592.5) * mm, "end": v(-183.74, 1592.5) * mm});
            skLineSegment(sketch, "E45.5", {"start": v(-400.25, 1717.5) * mm, "end": v(-328.08, 1592.5) * mm});
            skPoint(sketch, "E45.0.midPoint", {"position": v(-364.17, 1780) * mm});
            skCircle(sketch, "E46.cCircle", {"center": v(-255.91, 1452.5) * mm, "radius": 125 * mm, "construction": true});
            skLineSegment(sketch, "E46.0", {"start": v(-328.08, 1577.5) * mm, "end": v(-400.25, 1452.5) * mm});
            skLineSegment(sketch, "E46.1", {"start": v(-183.74, 1577.5) * mm, "end": v(-328.08, 1577.5) * mm});
            skLineSegment(sketch, "E46.2", {"start": v(-111.58, 1452.5) * mm, "end": v(-183.74, 1577.5) * mm});
            skLineSegment(sketch, "E46.3", {"start": v(-183.74, 1327.5) * mm, "end": v(-111.58, 1452.5) * mm});
            skLineSegment(sketch, "E46.4", {"start": v(-328.08, 1327.5) * mm, "end": v(-183.74, 1327.5) * mm});
            skLineSegment(sketch, "E46.5", {"start": v(-400.25, 1452.5) * mm, "end": v(-328.08, 1327.5) * mm});
            skPoint(sketch, "E46.0.midPoint", {"position": v(-364.17, 1515) * mm});
            skCircle(sketch, "E47.cCircle", {"center": v(-26.42, 1320) * mm, "radius": 125 * mm, "construction": true});
            skLineSegment(sketch, "E47.0", {"start": v(-98.58, 1445) * mm, "end": v(-170.75, 1320) * mm});
            skLineSegment(sketch, "E47.1", {"start": v(45.75, 1445) * mm, "end": v(-98.58, 1445) * mm});
            skLineSegment(sketch, "E47.2", {"start": v(117.92, 1320) * mm, "end": v(45.75, 1445) * mm});
            skLineSegment(sketch, "E47.3", {"start": v(45.75, 1195) * mm, "end": v(117.92, 1320) * mm});
            skLineSegment(sketch, "E47.4", {"start": v(-98.58, 1195) * mm, "end": v(45.75, 1195) * mm});
            skLineSegment(sketch, "E47.5", {"start": v(-170.75, 1320) * mm, "end": v(-98.58, 1195) * mm});
            skPoint(sketch, "E47.0.midPoint", {"position": v(-134.67, 1382.5) * mm});
            skCircle(sketch, "E48.cCircle", {"center": v(-255.91, 1187.5) * mm, "radius": 125 * mm, "construction": true});
            skLineSegment(sketch, "E48.0", {"start": v(-328.08, 1312.5) * mm, "end": v(-400.25, 1187.5) * mm});
            skLineSegment(sketch, "E48.1", {"start": v(-183.74, 1312.5) * mm, "end": v(-328.08, 1312.5) * mm});
            skLineSegment(sketch, "E48.2", {"start": v(-111.58, 1187.5) * mm, "end": v(-183.74, 1312.5) * mm});
            skLineSegment(sketch, "E48.3", {"start": v(-183.74, 1062.5) * mm, "end": v(-111.58, 1187.5) * mm});
            skLineSegment(sketch, "E48.4", {"start": v(-328.08, 1062.5) * mm, "end": v(-183.74, 1062.5) * mm});
            skLineSegment(sketch, "E48.5", {"start": v(-400.25, 1187.5) * mm, "end": v(-328.08, 1062.5) * mm});
            skPoint(sketch, "E48.0.midPoint", {"position": v(-364.17, 1250) * mm});
            skCircle(sketch, "E49.cCircle", {"center": v(-26.42, 1055) * mm, "radius": 125 * mm, "construction": true});
            skLineSegment(sketch, "E49.0", {"start": v(-98.58, 1180) * mm, "end": v(-170.75, 1055) * mm});
            skLineSegment(sketch, "E49.1", {"start": v(45.75, 1180) * mm, "end": v(-98.58, 1180) * mm});
            skLineSegment(sketch, "E49.2", {"start": v(117.92, 1055) * mm, "end": v(45.75, 1180) * mm});
            skLineSegment(sketch, "E49.3", {"start": v(45.75, 930) * mm, "end": v(117.92, 1055) * mm});
            skLineSegment(sketch, "E49.4", {"start": v(-98.58, 930) * mm, "end": v(45.75, 930) * mm});
            skLineSegment(sketch, "E49.5", {"start": v(-170.75, 1055) * mm, "end": v(-98.58, 930) * mm});
            skPoint(sketch, "E49.0.midPoint", {"position": v(-134.67, 1117.5) * mm});
            skCircle(sketch, "E50.cCircle", {"center": v(-255.91, 922.5) * mm, "radius": 125 * mm, "construction": true});
            skLineSegment(sketch, "E50.0", {"start": v(-328.08, 1047.5) * mm, "end": v(-400.25, 922.5) * mm});
            skLineSegment(sketch, "E50.1", {"start": v(-183.74, 1047.5) * mm, "end": v(-328.08, 1047.5) * mm});
            skLineSegment(sketch, "E50.2", {"start": v(-111.58, 922.5) * mm, "end": v(-183.74, 1047.5) * mm});
            skLineSegment(sketch, "E50.3", {"start": v(-183.74, 797.5) * mm, "end": v(-111.58, 922.5) * mm});
            skLineSegment(sketch, "E50.4", {"start": v(-328.08, 797.5) * mm, "end": v(-183.74, 797.5) * mm});
            skLineSegment(sketch, "E50.5", {"start": v(-400.25, 922.5) * mm, "end": v(-328.08, 797.5) * mm});
            skPoint(sketch, "E50.0.midPoint", {"position": v(-364.17, 985) * mm});
            skCircle(sketch, "E51.cCircle", {"center": v(-357.42, 155) * mm, "radius": 125 * mm, "construction": true});
            skLineSegment(sketch, "E51.0", {"start": v(-429.6, 280) * mm, "end": v(-501.76, 155) * mm});
            skLineSegment(sketch, "E51.1", {"start": v(-285.25, 280) * mm, "end": v(-429.6, 280) * mm});
            skLineSegment(sketch, "E51.2", {"start": v(-213.08, 155) * mm, "end": v(-285.25, 280) * mm});
            skLineSegment(sketch, "E51.3", {"start": v(-285.25, 30) * mm, "end": v(-213.08, 155) * mm});
            skLineSegment(sketch, "E51.4", {"start": v(-429.6, 30) * mm, "end": v(-285.25, 30) * mm});
            skLineSegment(sketch, "E51.5", {"start": v(-501.76, 155) * mm, "end": v(-429.6, 30) * mm});
            skPoint(sketch, "E51.0.midPoint", {"position": v(-465.68, 217.5) * mm});
            skCircle(sketch, "E52.cCircle", {"center": v(-356.67, 420) * mm, "radius": 125 * mm, "construction": true});
            skLineSegment(sketch, "E52.0", {"start": v(-428.84, 545) * mm, "end": v(-501, 420) * mm});
            skLineSegment(sketch, "E52.1", {"start": v(-284.5, 545) * mm, "end": v(-428.84, 545) * mm});
            skLineSegment(sketch, "E52.2", {"start": v(-212.33, 420) * mm, "end": v(-284.5, 545) * mm});
            skLineSegment(sketch, "E52.3", {"start": v(-284.5, 295) * mm, "end": v(-212.33, 420) * mm});
            skLineSegment(sketch, "E52.4", {"start": v(-428.84, 295) * mm, "end": v(-284.5, 295) * mm});
            skLineSegment(sketch, "E52.5", {"start": v(-501, 420) * mm, "end": v(-428.84, 295) * mm});
            skPoint(sketch, "E52.0.midPoint", {"position": v(-464.92, 482.5) * mm});
            skLineSegment(sketch, "E53.bottom", {"start": v(-518.08, 650) * mm, "end": v(-118.08, 650) * mm});
            skLineSegment(sketch, "E53.top", {"start": v(-518.08, 570) * mm, "end": v(-118.08, 570) * mm});
            skLineSegment(sketch, "E53.left", {"start": v(-518.08, 650) * mm, "end": v(-518.08, 570) * mm});
            skLineSegment(sketch, "E53.right", {"start": v(-118.08, 650) * mm, "end": v(-118.08, 570) * mm});
            skLineSegment(sketch, "E54.bottom", {"start": v(-518.08, 755) * mm, "end": v(-118.08, 755) * mm});
            skLineSegment(sketch, "E54.top", {"start": v(-518.08, 675) * mm, "end": v(-118.08, 675) * mm});
            skLineSegment(sketch, "E54.left", {"start": v(-518.08, 755) * mm, "end": v(-518.08, 675) * mm});
            skLineSegment(sketch, "E54.right", {"start": v(-118.08, 755) * mm, "end": v(-118.08, 675) * mm});
            skLineSegment(sketch, "E55.bottom", {"start": v(-58.08, 750) * mm, "end": v(111.92, 750) * mm});
            skLineSegment(sketch, "E55.top", {"start": v(-58.08, 560) * mm, "end": v(111.92, 560) * mm});
            skLineSegment(sketch, "E55.left", {"start": v(-58.08, 750) * mm, "end": v(-58.08, 560) * mm});
            skLineSegment(sketch, "E55.right", {"start": v(111.92, 750) * mm, "end": v(111.92, 560) * mm});
            skLineSegment(sketch, "E56.bottom", {"start": v(151.92, 560) * mm, "end": v(551.92, 560) * mm});
            skLineSegment(sketch, "E56.top", {"start": v(151.92, 615) * mm, "end": v(551.92, 615) * mm});
            skLineSegment(sketch, "E56.left", {"start": v(151.92, 560) * mm, "end": v(151.92, 615) * mm});
            skLineSegment(sketch, "E56.right", {"start": v(551.92, 560) * mm, "end": v(551.92, 615) * mm});
            skLineSegment(sketch, "E57.bottom", {"start": v(151.92, 695) * mm, "end": v(551.92, 695) * mm});
            skLineSegment(sketch, "E57.top", {"start": v(151.92, 640) * mm, "end": v(551.92, 640) * mm});
            skLineSegment(sketch, "E57.left", {"start": v(151.92, 695) * mm, "end": v(151.92, 640) * mm});
            skLineSegment(sketch, "E57.right", {"start": v(551.92, 695) * mm, "end": v(551.92, 640) * mm});
            skArc(sketch, "E58.cCircle", {"start": v(-377.16, 1647.5) * mm, "mid": v(-377.16, 1522.5) * mm, "end": v(-485.4, 1460) * mm, "construction": true});
            skLineSegment(sketch, "E58.1", {"start": v(-413.24, 1710) * mm, "end": v(-557.58, 1710) * mm});
            skLineSegment(sketch, "E58.2", {"start": v(-341.07, 1585) * mm, "end": v(-413.24, 1710) * mm});
            skLineSegment(sketch, "E58.3", {"start": v(-413.24, 1460) * mm, "end": v(-341.07, 1585) * mm});
            skLineSegment(sketch, "E58.4", {"start": v(-557.58, 1460) * mm, "end": v(-413.24, 1460) * mm});
            skPoint(sketch, "E58.0.midPoint", {"position": v(-593.66, 1647.5) * mm});
            skArc(sketch, "E59.cCircle", {"start": v(-557.58, 1952.06) * mm, "mid": v(-360.4, 1850) * mm, "end": v(-557.58, 1747.94) * mm, "construction": true});
            skLineSegment(sketch, "E59.1", {"start": v(-413.24, 1975) * mm, "end": v(-557.58, 1975) * mm});
            skLineSegment(sketch, "E59.2", {"start": v(-341.07, 1850) * mm, "end": v(-413.24, 1975) * mm});
            skLineSegment(sketch, "E59.3", {"start": v(-413.24, 1725) * mm, "end": v(-341.07, 1850) * mm});
            skLineSegment(sketch, "E59.4", {"start": v(-557.58, 1725) * mm, "end": v(-413.24, 1725) * mm});
            skPoint(sketch, "E59.0.midPoint", {"position": v(-593.66, 1912.5) * mm});
            skArc(sketch, "E60.cCircle", {"start": v(-557.58, 1422.06) * mm, "mid": v(-366.28, 1357.86) * mm, "end": v(-485.4, 1195) * mm, "construction": true});
            skLineSegment(sketch, "E60.1", {"start": v(-413.24, 1445) * mm, "end": v(-557.58, 1445) * mm});
            skLineSegment(sketch, "E60.2", {"start": v(-341.07, 1320) * mm, "end": v(-413.24, 1445) * mm});
            skLineSegment(sketch, "E60.3", {"start": v(-413.24, 1195) * mm, "end": v(-341.07, 1320) * mm});
            skLineSegment(sketch, "E60.4", {"start": v(-557.58, 1195) * mm, "end": v(-413.24, 1195) * mm});
            skPoint(sketch, "E60.0.midPoint", {"position": v(-593.66, 1382.5) * mm});
            skArc(sketch, "E61.cCircle", {"start": v(-485.4, 1180) * mm, "mid": v(-366.28, 1017.14) * mm, "end": v(-557.58, 952.94) * mm, "construction": true});
            skLineSegment(sketch, "E61.1", {"start": v(-413.24, 1180) * mm, "end": v(-557.58, 1180) * mm});
            skLineSegment(sketch, "E61.2", {"start": v(-341.07, 1055) * mm, "end": v(-413.24, 1180) * mm});
            skLineSegment(sketch, "E61.3", {"start": v(-413.24, 930) * mm, "end": v(-341.07, 1055) * mm});
            skLineSegment(sketch, "E61.4", {"start": v(-557.58, 930) * mm, "end": v(-413.24, 930) * mm});
            skPoint(sketch, "E61.0.midPoint", {"position": v(-593.66, 1117.5) * mm});
            skLineSegment(sketch, "E62", {"start": v(-557.58, 1975) * mm, "end": v(-557.58, 1725) * mm});
            skLineSegment(sketch, "E63.trimOffspring", {"start": v(-557.58, 952.94) * mm, "end": v(-557.58, 930) * mm});
            skPoint(sketch, "E61.0.start.orphan", {"position": v(-629.75, 1055) * mm});
            skPoint(sketch, "E64.orphan", {"position": v(-629.75, 1320) * mm});
            skPoint(sketch, "E65.orphan", {"position": v(-629.75, 1585) * mm});
            skPoint(sketch, "E59.5.end.orphan", {"position": v(-629.75, 1850) * mm});
            skLineSegment(sketch, "E66.trimOffspring", {"start": v(-557.58, 1710) * mm, "end": v(-557.58, 1460) * mm});
            skLineSegment(sketch, "E67.trimOffspring", {"start": v(-557.58, 1445) * mm, "end": v(-557.58, 1195) * mm});
            skLineSegment(sketch, "E68.trimOffspring", {"start": v(-557.58, 1180) * mm, "end": v(-557.58, 1157.06) * mm});
            skLineSegment(sketch, "E69", {"start": v(-557.58, 1157.06) * mm, "end": v(-557.58, 952.94) * mm});
            skSolve(sketch);
        }
        {
            var Q0;
            Q0 = qSketchRegion(id + "F65", true);
            extrude(context, id + "F66", {"entities" : qUnion([Q0]), "operationType" : NewBodyOperationType.REMOVE, "oppositeDirection" : true, "depth" : 220 * mm, "offsetDistance" : 25 * mm});
        }
        {
            var Q0;
            Q0=makeQuery(id+"F66.boolean.opBoolean","COPY",FACE,{"derivedFrom":makeQuery(id+"F66.opExtrude","CAP_FACE",FACE,{"disambiguationData":[OSD([sQuery(id+"F65.wireOp",EDGE,"E54.bottom"),sQuery(id+"F65.wireOp",EDGE,"E54.top"),sQuery(id+"F65.wireOp",EDGE,"E54.left"),sQuery(id+"F65.wireOp",EDGE,"E54.right")])],"isStart":false})});
            var sketch = newSketch(context, id + "F67", { "sketchPlane" : qUnion([Q0])});
            skLineSegment(sketch, "E70.bottom", {"start": v(-518.08, 755) * mm, "end": v(-118.08, 755) * mm});
            skLineSegment(sketch, "E70.top", {"start": v(-518.08, 675) * mm, "end": v(-118.08, 675) * mm});
            skLineSegment(sketch, "E70.left", {"start": v(-518.08, 755) * mm, "end": v(-518.08, 675) * mm});
            skLineSegment(sketch, "E70.right", {"start": v(-118.08, 755) * mm, "end": v(-118.08, 675) * mm});
            skLineSegment(sketch, "E71.bottom", {"start": v(-58.08, 750) * mm, "end": v(111.92, 750) * mm});
            skLineSegment(sketch, "E71.top", {"start": v(-58.08, 560) * mm, "end": v(111.92, 560) * mm});
            skLineSegment(sketch, "E71.left", {"start": v(-58.08, 750) * mm, "end": v(-58.08, 560) * mm});
            skLineSegment(sketch, "E71.right", {"start": v(111.92, 750) * mm, "end": v(111.92, 560) * mm});
            skLineSegment(sketch, "E72.bottom", {"start": v(151.92, 695) * mm, "end": v(551.92, 695) * mm});
            skLineSegment(sketch, "E72.top", {"start": v(151.92, 640) * mm, "end": v(551.92, 640) * mm});
            skLineSegment(sketch, "E72.left", {"start": v(151.92, 695) * mm, "end": v(151.92, 640) * mm});
            skLineSegment(sketch, "E72.right", {"start": v(551.92, 695) * mm, "end": v(551.92, 640) * mm});
            skLineSegment(sketch, "E73.bottom", {"start": v(551.92, 615) * mm, "end": v(151.92, 615) * mm});
            skLineSegment(sketch, "E73.top", {"start": v(551.92, 560) * mm, "end": v(151.92, 560) * mm});
            skLineSegment(sketch, "E73.left", {"start": v(551.92, 615) * mm, "end": v(551.92, 560) * mm});
            skLineSegment(sketch, "E73.right", {"start": v(151.92, 615) * mm, "end": v(151.92, 560) * mm});
            skLineSegment(sketch, "E74.bottom", {"start": v(-118.08, 650) * mm, "end": v(-518.08, 650) * mm});
            skLineSegment(sketch, "E74.top", {"start": v(-118.08, 570) * mm, "end": v(-518.08, 570) * mm});
            skLineSegment(sketch, "E74.left", {"start": v(-118.08, 650) * mm, "end": v(-118.08, 570) * mm});
            skLineSegment(sketch, "E74.right", {"start": v(-518.08, 650) * mm, "end": v(-518.08, 570) * mm});
            skSolve(sketch);
        }
        {
            var Q0;
            Q0 = qSketchRegion(id + "F67", true);
            extrude(context, id + "F68", {"entities" : qUnion([Q0]), "operationType" : NewBodyOperationType.ADD, "depth" : 70 * mm, "offsetDistance" : 25 * mm});
        }
        {
            var Q0;
            Q0=makeQuery(id+"F1.opExtrude","CAP_FACE",FACE,{"disambiguationData":[OSD([sQuery(id+"F0.wireOp",EDGE,"E0.bottom"),sQuery(id+"F0.wireOp",EDGE,"E0.top"),sQuery(id+"F0.wireOp",EDGE,"E0.left"),sQuery(id+"F0.wireOp",EDGE,"E0.right")])],"isStart":true});
            cPlane(context, id + "F69", {"entities" : qUnion([Q0]), "cplaneType" : CPlaneType.OFFSET, "offset" : 1000 * mm, "oppositeDirection" : true, "width" : 150 * mm, "height" : 150 * mm});
        }
        {
            var Q0;
            Q0=makeQuery(id+"F1.opExtrude","SWEPT_FACE",FACE,{"disambiguationData":[OSD([sQuery(id+"F0.wireOp",EDGE,"E0.right")])]});
            var sketch = newSketch(context, id + "F70", { "sketchPlane" : qUnion([Q0])});
            skLineSegment(sketch, "E75.bottom", {"start": v(-18.95, 1025) * mm, "end": v(6.05, 1025) * mm});
            skLineSegment(sketch, "E75.top", {"start": v(-18.95, 975) * mm, "end": v(6.05, 975) * mm});
            skLineSegment(sketch, "E75.left", {"start": v(-18.95, 1025) * mm, "end": v(-18.95, 975) * mm});
            skLineSegment(sketch, "E75.right", {"start": v(6.05, 1025) * mm, "end": v(6.05, 975) * mm});
            skSolve(sketch);
        }
        {
            var Q0;
            Q0 = qSketchRegion(id + "F70", true);
            extrude(context, id + "F71", {"entities" : qUnion([Q0]), "operationType" : NewBodyOperationType.ADD, "depth" : 25 * mm, "offsetDistance" : 25 * mm});
        }
        {
            var Q0;
            Q0=makeQuery(id+"F71.opExtrude","SWEPT_FACE",FACE,{"disambiguationData":[OSD([sQuery(id+"F70.wireOp",EDGE,"E75.left")])]});
            var sketch = newSketch(context, id + "F72", { "sketchPlane" : qUnion([Q0])});
            skLineSegment(sketch, "E76.bottom", {"start": v(606.92, 1012.5) * mm, "end": v(623.92, 1012.5) * mm});
            skLineSegment(sketch, "E76.top", {"start": v(606.92, 987.5) * mm, "end": v(623.92, 987.5) * mm});
            skLineSegment(sketch, "E76.left", {"start": v(606.92, 1012.5) * mm, "end": v(606.92, 987.5) * mm});
            skLineSegment(sketch, "E76.right", {"start": v(623.92, 1012.5) * mm, "end": v(623.92, 987.5) * mm});
            skSolve(sketch);
        }
        {
            var Q0;
            Q0=makeQuery(id+"F72.imprint","IMPRINT",FACE,{"disambiguationData":[TD([[makeQuery(id+"F72.imprint","IMPRINT",EDGE,{"derivedFrom":sQuery(id+"F72.wireOp",EDGE,"E76.bottom")}),-1.0]])]});
            extrude(context, id + "F73", {"entities" : qUnion([Q0]), "operationType" : NewBodyOperationType.REMOVE, "oppositeDirection" : true, "depth" : 230 * mm, "offsetDistance" : 25 * mm});
        }
        {
            var Q0;
            Q0=makeQuery(id+"F71.opExtrude","CAP_EDGE",EDGE,{"disambiguationData":[OSD([sQuery(id+"F70.wireOp",EDGE,"E75.bottom")])],"isStart":false});
            var Q1;
            Q1=makeQuery(id+"F71.opExtrude","CAP_EDGE",EDGE,{"disambiguationData":[OSD([sQuery(id+"F70.wireOp",EDGE,"E75.top")])],"isStart":false});
            var Q2;
            Q2=makeQuery(id+"F73.boolean.opBoolean","COPY",EDGE,{"derivedFrom":makeQuery(id+"F73.opExtrude","SWEPT_EDGE",EDGE,{"disambiguationData":[OSD([sQuery(id+"F72.wireOp",EDGE,"E76.bottom"),sQuery(id+"F72.wireOp",EDGE,"E76.right")])]})});
            var Q3;
            Q3=makeQuery(id+"F73.boolean.opBoolean","COPY",EDGE,{"derivedFrom":makeQuery(id+"F73.opExtrude","SWEPT_EDGE",EDGE,{"disambiguationData":[OSD([sQuery(id+"F72.wireOp",EDGE,"E76.top"),sQuery(id+"F72.wireOp",EDGE,"E76.right")])]})});
            fillet(context, id + "F74", {"entities" : qUnion([Q0, Q1, Q2, Q3]), "radius" : 5 * mm, "tangentPropagation" : true, "allowEdgeOverflow" : false});
        }
    });
